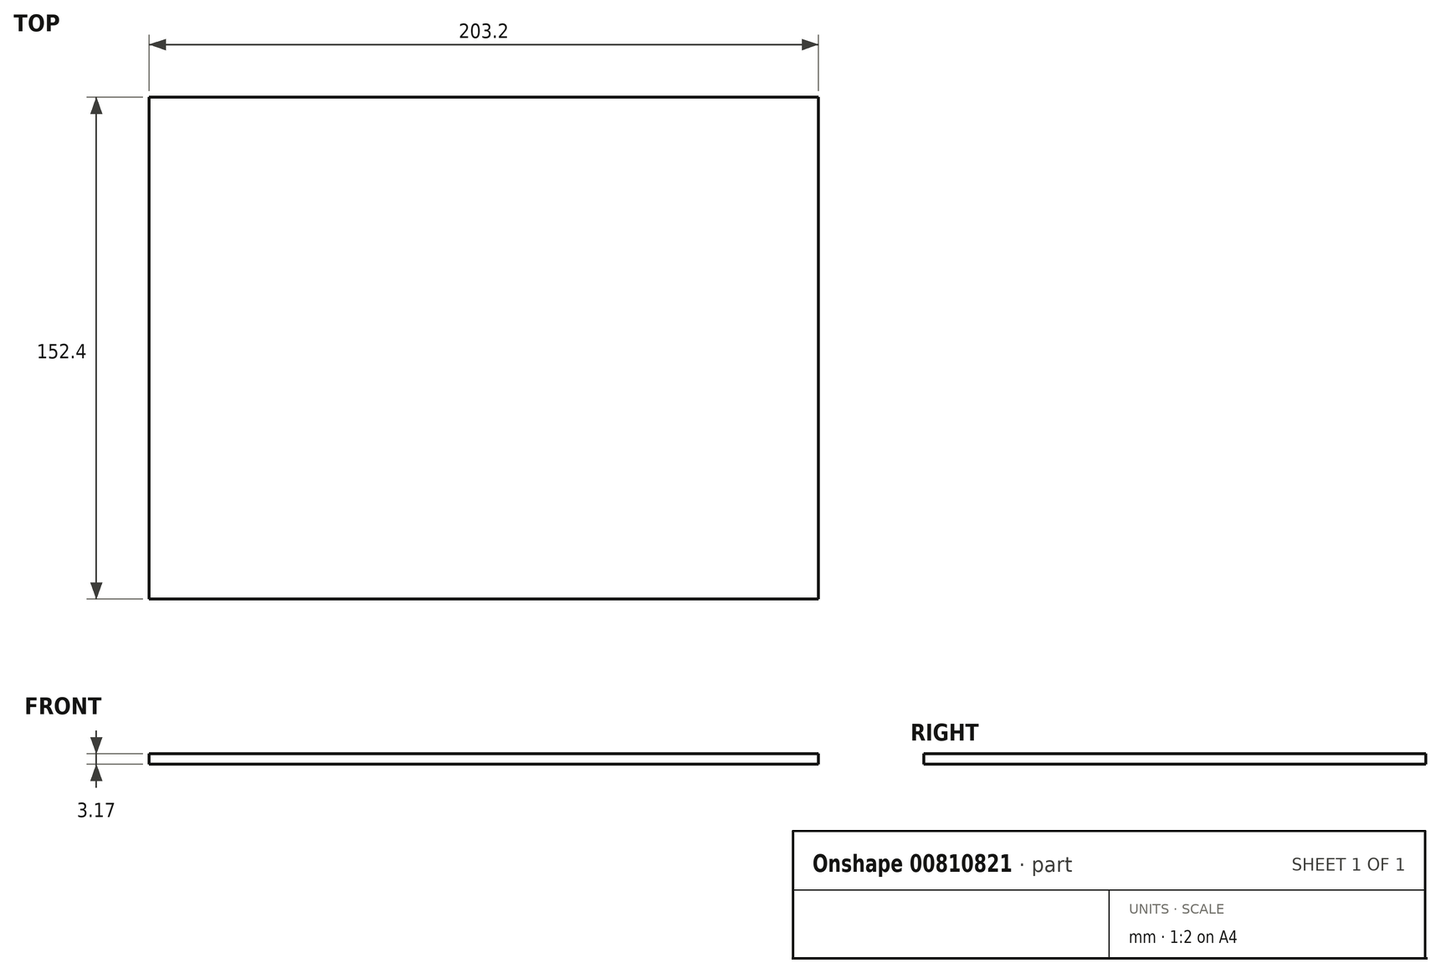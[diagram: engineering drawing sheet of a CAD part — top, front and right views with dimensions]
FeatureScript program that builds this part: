
annotation { "Feature Type Name" : "Feature", "Feature Type Description" : "" }
export const myFeature = defineFeature(function(context is Context, id is Id, definition is map)
    precondition{}
    {
        {
            var Q0;
            Q0=qCreatedBy(makeId("Top.planeOp"),FACE);
            var sketch = newSketch(context, id + "F0", { "sketchPlane" : qUnion([Q0])});
            skLineSegment(sketch, "E0.bottom", {"start": v(-46.74, 77.27) * mm, "end": v(156.46, 77.27) * mm});
            skLineSegment(sketch, "E0.top", {"start": v(-46.74, -75.13) * mm, "end": v(156.46, -75.13) * mm});
            skLineSegment(sketch, "E0.left", {"start": v(-46.74, 77.27) * mm, "end": v(-46.74, -75.13) * mm});
            skLineSegment(sketch, "E0.right", {"start": v(156.46, 77.27) * mm, "end": v(156.46, -75.13) * mm});
            skSolve(sketch);
        }
        {
            var Q0;
            Q0 = qSketchRegion(id + "F0", true);
            extrude(context, id + "F1", {"entities" : qUnion([Q0]), "depth" : 3.17 * mm, "offsetDistance" : 25.4 * mm});
        }
    });
